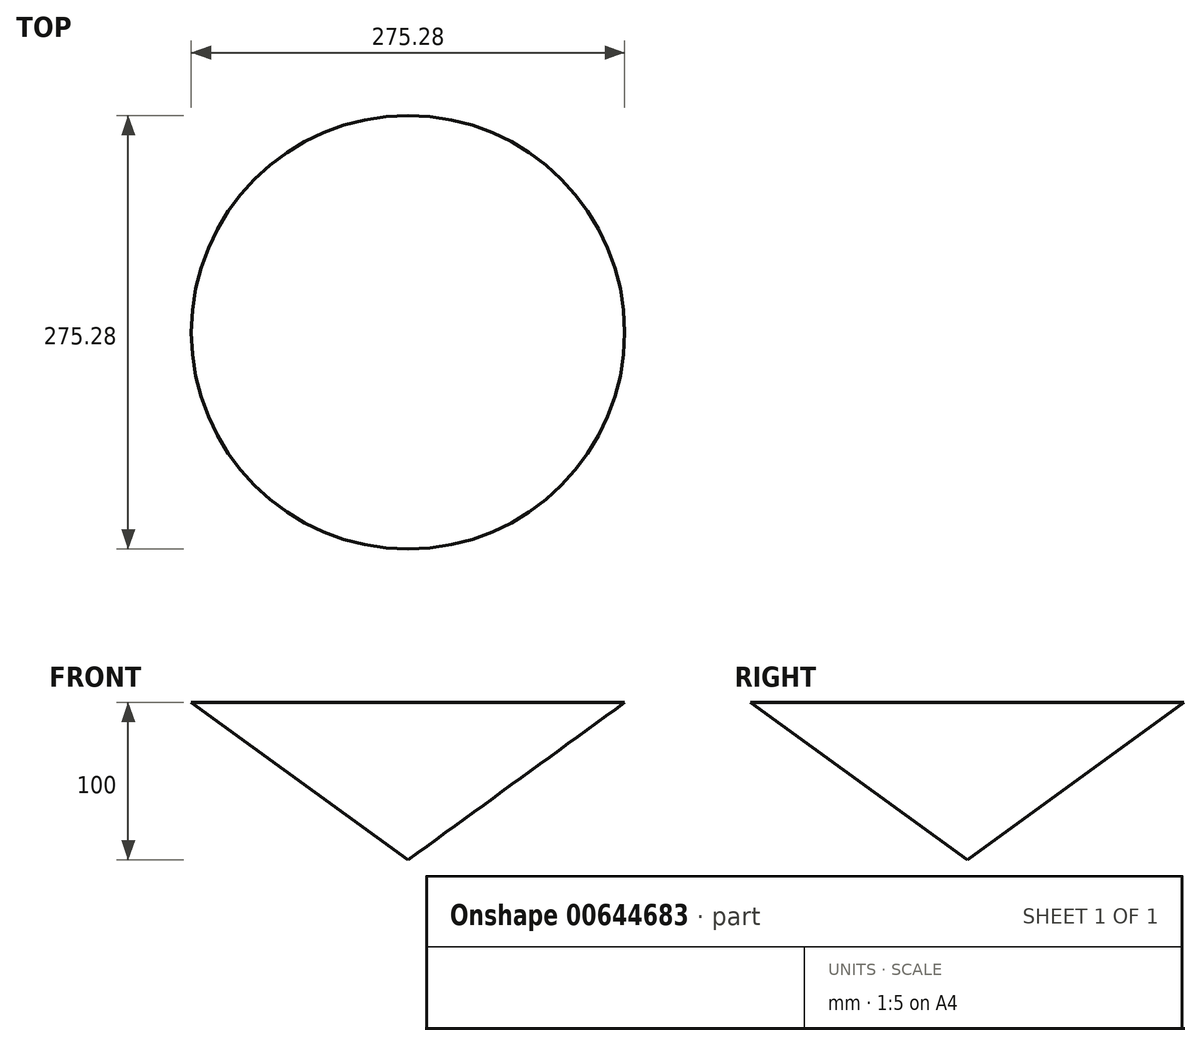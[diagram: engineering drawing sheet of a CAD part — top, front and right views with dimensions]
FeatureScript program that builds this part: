
annotation { "Feature Type Name" : "Feature", "Feature Type Description" : "" }
export const myFeature = defineFeature(function(context is Context, id is Id, definition is map)
    precondition{}
    {
        {
            var Q0;
            Q0=qCreatedBy(makeId("Front.planeOp"),FACE);
            var sketch = newSketch(context, id + "F0", { "sketchPlane" : qUnion([Q0])});
            skLineSegment(sketch, "E0", {"start": v(0, 0) * mm, "end": v(0, 100) * mm});
            skLineSegment(sketch, "E1", {"start": v(0, 100) * mm, "end": v(-137.64, 100) * mm});
            skLineSegment(sketch, "E2", {"start": v(-137.64, 100) * mm, "end": v(0, 0) * mm});
            skSolve(sketch);
        }
        {
            var Q0;
            Q0=makeQuery(id+"F0.imprint","IMPRINT",FACE,{"disambiguationData":[TD([[makeQuery(id+"F0.imprint","IMPRINT",EDGE,{"derivedFrom":sQuery(id+"F0.wireOp",EDGE,"E0")}),1.0]])]});
            var Q1;
            Q1=sQuery(id+"F0.wireOp",EDGE,"E0");
            revolve(context, id + "F1", {"entities" : qUnion([Q0]), "axis" : qUnion([Q1]), "revolveType" : RevolveType.FULL});
        }
    });
